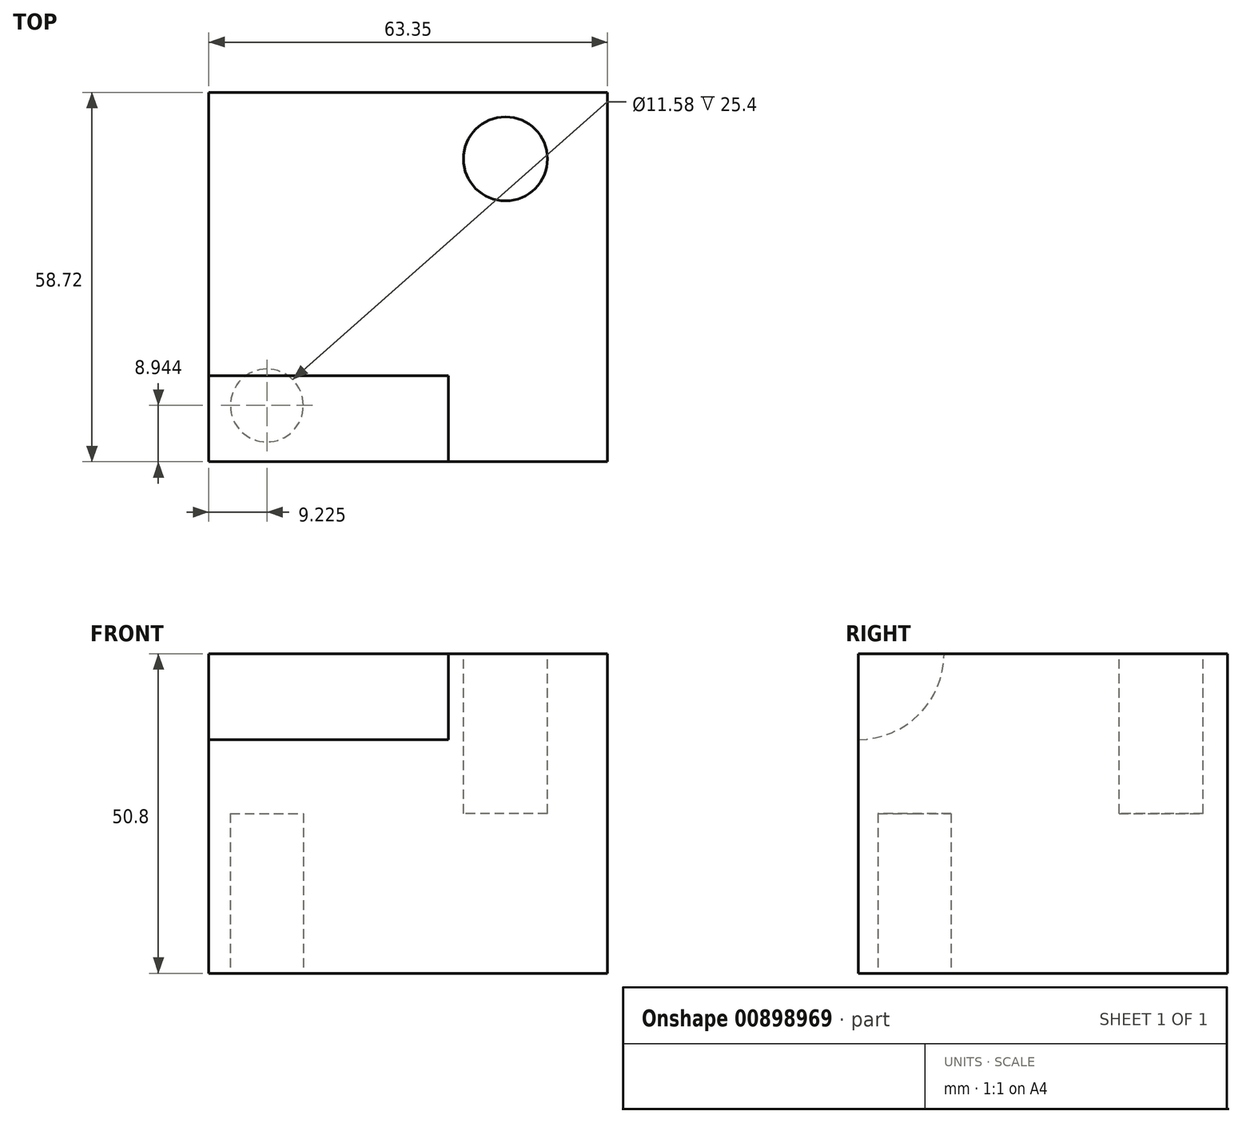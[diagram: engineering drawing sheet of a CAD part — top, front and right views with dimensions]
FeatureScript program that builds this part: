
annotation { "Feature Type Name" : "Feature", "Feature Type Description" : "" }
export const myFeature = defineFeature(function(context is Context, id is Id, definition is map)
    precondition{}
    {
        {
            var Q0;
            Q0=qCreatedBy(makeId("Top.planeOp"),FACE);
            var sketch = newSketch(context, id + "F0", { "sketchPlane" : qUnion([Q0])});
            skLineSegment(sketch, "E0.bottom", {"start": v(0, 0) * mm, "end": v(63.35, 0) * mm});
            skLineSegment(sketch, "E0.top", {"start": v(0, 58.72) * mm, "end": v(63.35, 58.72) * mm});
            skLineSegment(sketch, "E0.left", {"start": v(0, 0) * mm, "end": v(0, 58.72) * mm});
            skLineSegment(sketch, "E0.right", {"start": v(63.35, 0) * mm, "end": v(63.35, 58.72) * mm});
            skSolve(sketch);
        }
        {
            var Q0;
            Q0 = qSketchRegion(id + "F0", true);
            extrude(context, id + "F1", {"entities" : qUnion([Q0]), "depth" : 50.8 * mm, "offsetDistance" : 25.4 * mm});
        }
        {
            var Q0;
            Q0=makeQuery(id+"F1.opExtrude","CAP_FACE",FACE,{"disambiguationData":[OSD([sQuery(id+"F0.wireOp",EDGE,"E0.bottom"),sQuery(id+"F0.wireOp",EDGE,"E0.top"),sQuery(id+"F0.wireOp",EDGE,"E0.left"),sQuery(id+"F0.wireOp",EDGE,"E0.right")])],"isStart":false});
            var sketch = newSketch(context, id + "F2", { "sketchPlane" : qUnion([Q0])});
            skCircle(sketch, "E1", {"center": v(47.15, 48.13) * mm, "radius": 6.68 * mm});
            skSolve(sketch);
        }
        {
            var Q0;
            Q0 = qSketchRegion(id + "F2", true);
            extrude(context, id + "F3", {"entities" : qUnion([Q0]), "operationType" : NewBodyOperationType.REMOVE, "oppositeDirection" : true, "depth" : 25.4 * mm, "offsetDistance" : 25.4 * mm});
        }
        {
            var Q0;
            Q0=makeQuery(id+"F1.opExtrude","CAP_FACE",FACE,{"disambiguationData":[OSD([sQuery(id+"F0.wireOp",EDGE,"E0.bottom"),sQuery(id+"F0.wireOp",EDGE,"E0.top"),sQuery(id+"F0.wireOp",EDGE,"E0.left"),sQuery(id+"F0.wireOp",EDGE,"E0.right")])],"isStart":true});
            var sketch = newSketch(context, id + "F4", { "sketchPlane" : qUnion([Q0])});
            skCircle(sketch, "E2", {"center": v(9.23, -8.94) * mm, "radius": 5.79 * mm});
            skSolve(sketch);
        }
        {
            var Q0;
            Q0 = qSketchRegion(id + "F4", true);
            extrude(context, id + "F5", {"entities" : qUnion([Q0]), "operationType" : NewBodyOperationType.REMOVE, "oppositeDirection" : true, "depth" : 25.4 * mm, "offsetDistance" : 25.4 * mm});
        }
        {
            var Q0;
            Q0=makeQuery(id+"F1.opExtrude","SWEPT_FACE",FACE,{"disambiguationData":[OSD([sQuery(id+"F0.wireOp",EDGE,"E0.left")])]});
            var sketch = newSketch(context, id + "F6", { "sketchPlane" : qUnion([Q0])});
            skCircle(sketch, "E3", {"center": v(0, 50.8) * mm, "radius": 13.65 * mm});
            skSolve(sketch);
        }
        {
            var Q0;
            Q0 = qSketchRegion(id + "F6", true);
            extrude(context, id + "F7", {"entities" : qUnion([Q0]), "operationType" : NewBodyOperationType.REMOVE, "oppositeDirection" : true, "depth" : 38.1 * mm, "offsetDistance" : 25.4 * mm});
        }
    });
